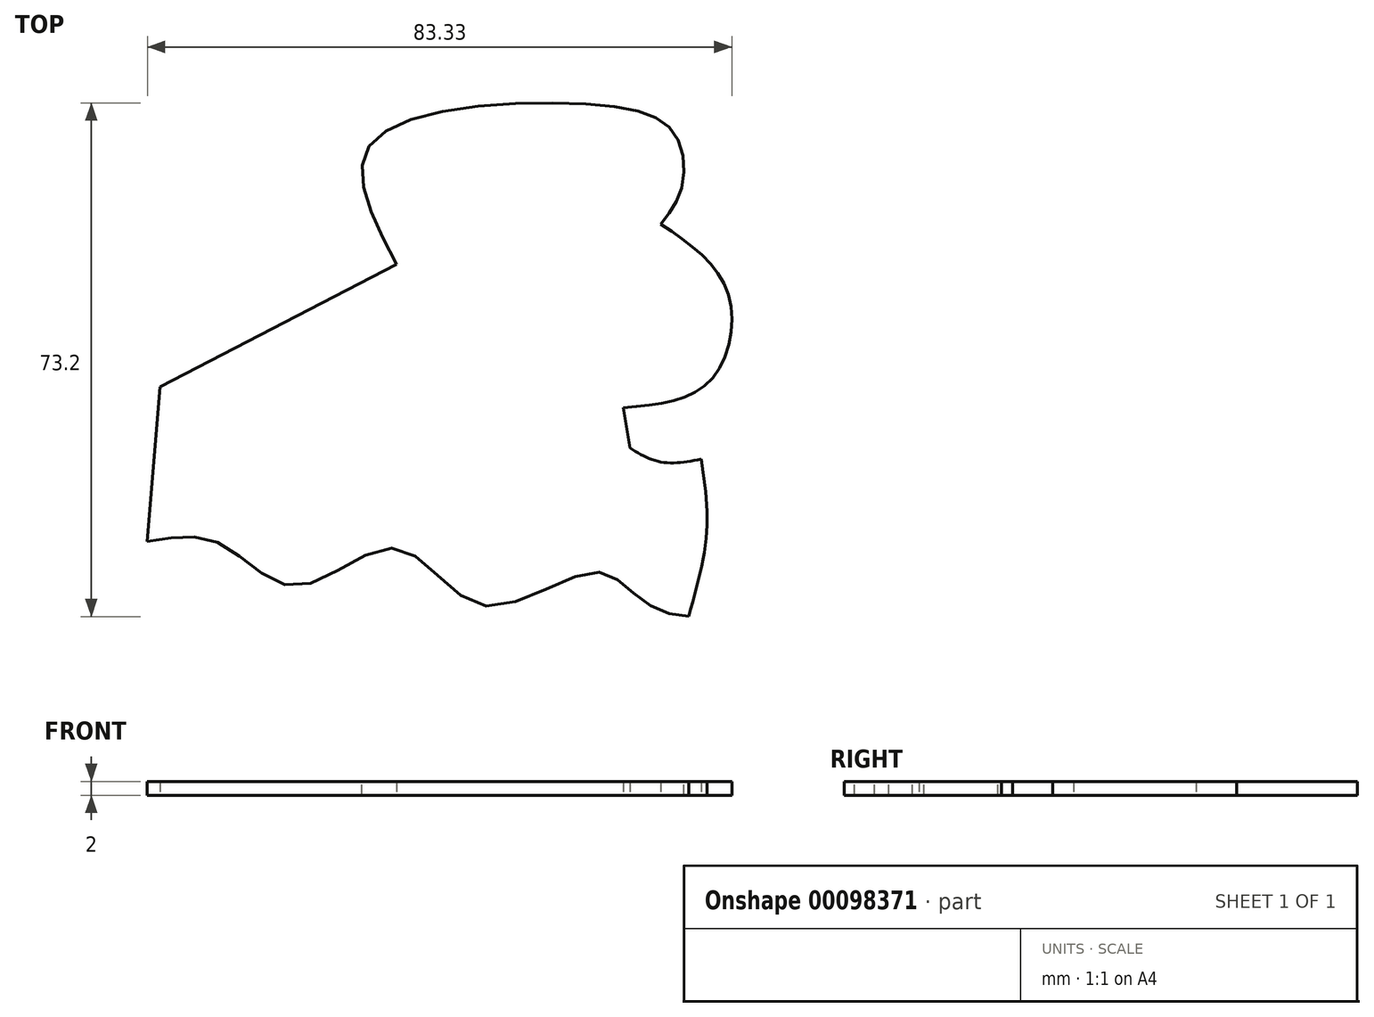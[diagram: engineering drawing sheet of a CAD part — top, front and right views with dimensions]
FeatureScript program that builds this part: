
annotation { "Feature Type Name" : "Feature", "Feature Type Description" : "" }
export const myFeature = defineFeature(function(context is Context, id is Id, definition is map)
    precondition{}
    {
        {
            var Q0;
            Q0=qCreatedBy(makeId("Top.planeOp"), FACE);
            var sketch = newSketch(context, id + "F0", { "sketchPlane" : qUnion([Q0])});
            skFitSpline(sketch, "E0", {"points": [v(-10.31, 14.78) * mm, v(-13.89, 32.04) * mm, v(17.26, 37.59) * mm, v(29.36, 33.42) * mm, v(30.35, 25.69) * mm, v(27.37, 20.53) * mm], "startDerivative": vector(-45.85, 88) * mm, "endDerivative": vector(-27.66, -34.9) * mm});
            skFitSpline(sketch, "E1", {"points": [v(27.37, 20.53) * mm, v(36.9, 10.81) * mm, v(34.32, -1.88) * mm, v(22.02, -5.65) * mm], "startDerivative": vector(35.75, -24.22) * mm, "endDerivative": vector(-42.78, -3.63) * mm});
            skFitSpline(sketch, "E2", {"points": [v(22.02, -5.65) * mm, v(23.01, -11.4) * mm], "startDerivative": vector(1, -5.75) * mm, "endDerivative": vector(1, -5.75) * mm});
            skFitSpline(sketch, "E3", {"points": [v(23.01, -11.4) * mm, v(27.37, -13.39) * mm, v(33.13, -13) * mm], "startDerivative": vector(8.7, -5.33) * mm, "endDerivative": vector(11.48, 2.04) * mm});
            skFitSpline(sketch, "E4", {"points": [v(33.13, -13) * mm, v(33.92, -23.3) * mm, v(31.34, -35.4) * mm], "startDerivative": vector(3.24, -21.22) * mm, "endDerivative": vector(-6.66, -23.58) * mm});
            skFitSpline(sketch, "E5", {"points": [v(31.34, -35.4) * mm, v(24.4, -32.83) * mm, v(17.85, -29.06) * mm, v(1.98, -33.82) * mm, v(-10.31, -25.69) * mm, v(-24.6, -31.04) * mm, v(-35.7, -24.9) * mm, v(-45.82, -24.7) * mm], "startDerivative": vector(-62.46, 0.79) * mm, "endDerivative": vector(-77.3, -10.63) * mm});
            skFitSpline(sketch, "E6", {"points": [v(-45.82, -24.7) * mm, v(-44.04, -2.68) * mm], "startDerivative": vector(1.79, 22.02) * mm, "endDerivative": vector(1.79, 22.02) * mm});
            skFitSpline(sketch, "E7", {"points": [v(-44.04, -2.68) * mm, v(-10.31, 14.78) * mm], "startDerivative": vector(33.72, 17.46) * mm, "endDerivative": vector(33.72, 17.46) * mm});
            skSolve(sketch);
        }
        {
            var Q0;
            Q0 = qSketchRegion(id + "F0", true);
            extrude(context, id + "F1", {"entities" : qUnion([Q0]), "depth" : 2 * mm, "offsetDistance" : 25 * mm});
        }
    });
